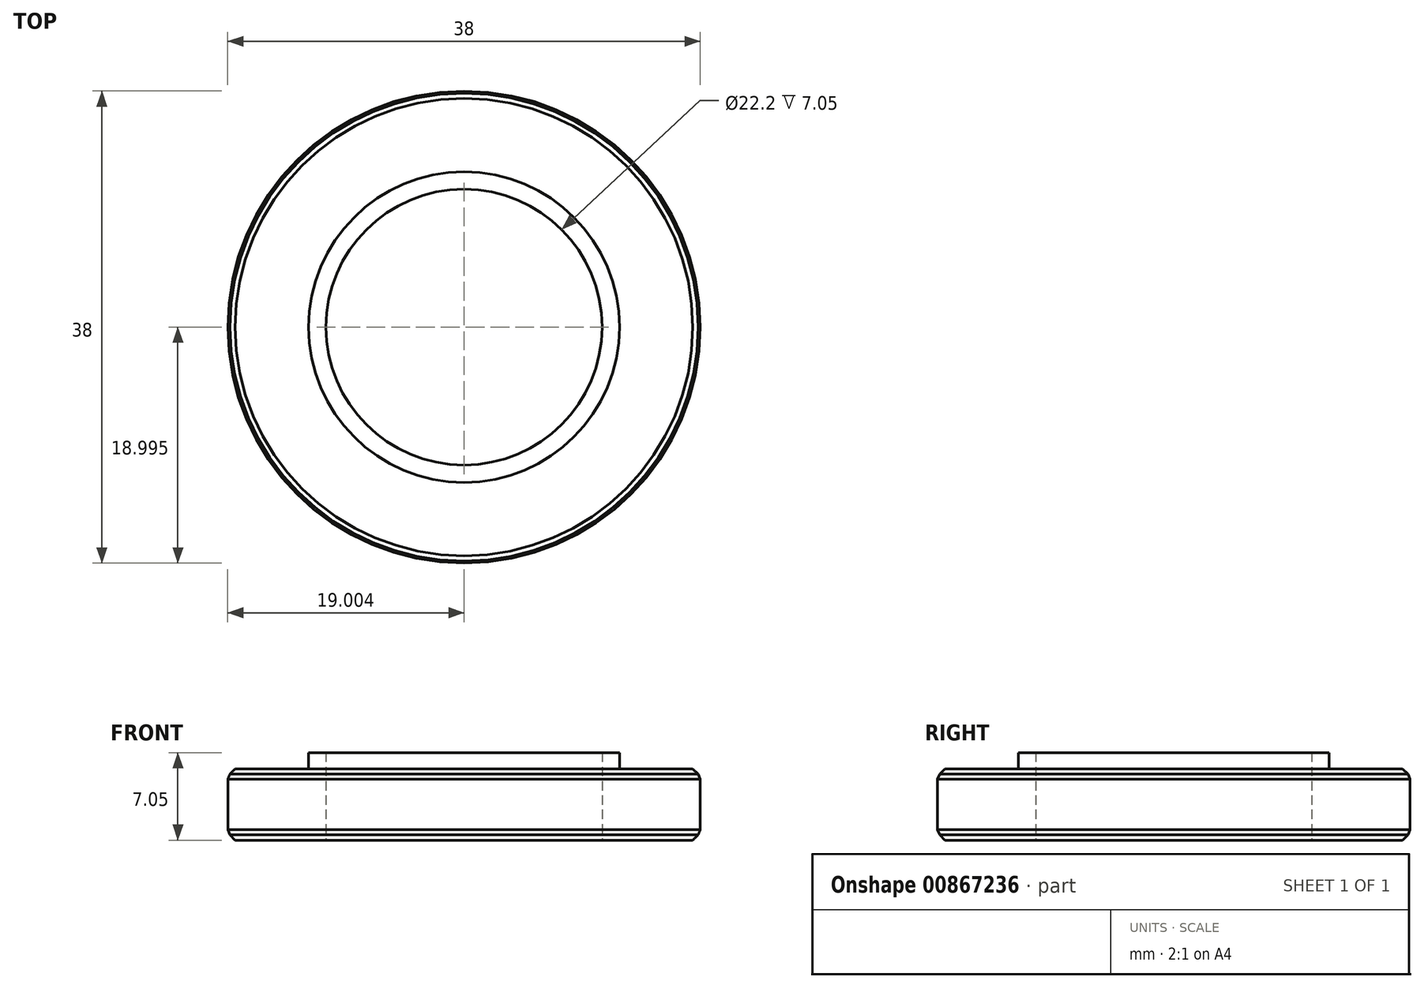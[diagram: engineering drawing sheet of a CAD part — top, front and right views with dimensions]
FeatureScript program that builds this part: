
annotation { "Feature Type Name" : "Feature", "Feature Type Description" : "" }
export const myFeature = defineFeature(function(context is Context, id is Id, definition is map)
    precondition{}
    {
        {
            var Q0;
            Q0=qCreatedBy(makeId("Top.planeOp"),FACE);
            var sketch = newSketch(context, id + "F0", { "sketchPlane" : qUnion([Q0])});
            skCircle(sketch, "E0", {"center": v(-89.73, 31.17) * mm, "radius": 11.1 * mm});
            skCircle(sketch, "E1.0", {"center": v(-89.73, 31.17) * mm, "radius": 19 * mm});
            skCircle(sketch, "E2.0", {"center": v(-89.73, 31.17) * mm, "radius": 12.5 * mm});
            skSolve(sketch);
        }
        {
            var Q0;
            Q0=makeQuery(id+"F0.imprint","IMPRINT",FACE,{"disambiguationData":[TD([[makeQuery(id+"F0.imprint","IMPRINT",EDGE,{"derivedFrom":sQuery(id+"F0.wireOp",EDGE,"E1.0")}),1.0]])]});
            extrude(context, id + "F1", {"entities" : qUnion([Q0]), "depth" : 5.75 * mm, "offsetDistance" : 25 * mm});
        }
        {
            var Q0;
            Q0=makeQuery(id+"F0.imprint","IMPRINT",FACE,{"disambiguationData":[TD([[makeQuery(id+"F0.imprint","IMPRINT",EDGE,{"derivedFrom":sQuery(id+"F0.wireOp",EDGE,"E0")}),-1.0]])]});
            extrude(context, id + "F2", {"entities" : qUnion([Q0]), "operationType" : NewBodyOperationType.ADD, "depth" : 7.05 * mm, "offsetDistance" : 25 * mm});
        }
        {
            var Q0;
            Q0=makeQuery(id+"F1.opExtrude","CAP_EDGE",EDGE,{"disambiguationData":[OSD([sQuery(id+"F0.wireOp",EDGE,"E1.0")])],"isStart":false});
            var Q1;
            Q1=makeQuery(id+"F1.opExtrude","CAP_EDGE",EDGE,{"disambiguationData":[OSD([sQuery(id+"F0.wireOp",EDGE,"E1.0")])],"isStart":true});
            chamfer(context, id + "F3", {"entities" : qUnion([Q0, Q1]), "width" : .6 * mm, "tangentPropagation" : true});
        }
        {
            var Q0;
            {var subQ0=sQuery(id+"F0.wireOp",EDGE,"E1.0");Q0=makeQuery(id+"F3.opChamfer","BLEND_EDGE",EDGE,{"blendedFrom":[makeQuery(id+"F1.opExtrude","CAP_EDGE",EDGE,{"disambiguationData":[OSD([subQ0])],"isStart":false}),makeQuery(id+"F1.opExtrude","SWEPT_FACE",FACE,{"disambiguationData":[OSD([subQ0])]})],"blendedInto":[makeQuery(id+"F1.opExtrude","SWEPT_FACE",FACE,{"disambiguationData":[OSD([subQ0])]})]});}
            var Q1;
            {var subQ0=sQuery(id+"F0.wireOp",EDGE,"E1.0");Q1=makeQuery(id+"F3.opChamfer","BLEND_EDGE",EDGE,{"blendedFrom":[makeQuery(id+"F1.opExtrude","CAP_EDGE",EDGE,{"disambiguationData":[OSD([subQ0])],"isStart":true}),makeQuery(id+"F1.opExtrude","SWEPT_FACE",FACE,{"disambiguationData":[OSD([subQ0])]})],"blendedInto":[makeQuery(id+"F1.opExtrude","SWEPT_FACE",FACE,{"disambiguationData":[OSD([subQ0])]})]});}
            chamfer(context, id + "F4", {"entities" : qUnion([Q0, Q1]), "width" : .6 * mm, "tangentPropagation" : true});
        }
    });
